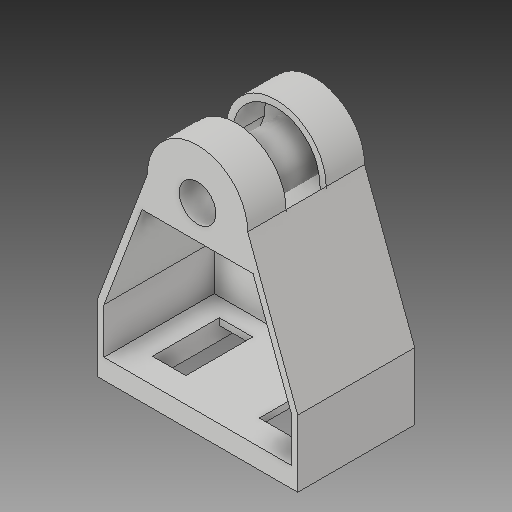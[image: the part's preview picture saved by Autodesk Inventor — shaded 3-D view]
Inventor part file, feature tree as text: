
AUTODESK INVENTOR PART (.ipt)
format: ipt  version: 2019 (Build 230136000, 136)  size: 250,368 bytes
history: native  units: mm
features: sketch x9, extrude x7, plane x2, shell x1, thicken_offset x1, hole x1, projected_geometry x1
ambient origin geometry x8: Origin, YZ Plane, XZ Plane, XY Plane, X Axis, Y Axis, Z Axis, Center Point
bodies: Solid1 (feature_tree)
feature tree (22):
  extrude  "Extrusion1"  Depth=5.5mm
  shell  "Shell2"  Thickness=17.5mm
  thicken_offset  "Thicken5"
  extrude  "Extrusion6"  Depth=30.0mm
  extrude  "Extrusion7"  Depth=2.0mm
  sketch  "Sketch14"  dims[d70=2.0mm d74=21.0mm]
  plane  "Work Plane2"
  hole  "Hole3"  [1 undecoded]
  extrude  "Extrusion9"  Depth=4.5mm
  extrude  "Extrusion10"  Depth=1.25mm
  plane  "Work Plane3"
  extrude  "Extrusion11"  Depth=5.0mm
  extrude  "Extrusion13"  Depth=2.5mm
  sketch  "Sketch1"  dims[d0=15.0mm d8=5.5mm d9=17.5mm d10=0.0mm]
  sketch  "Sketch12"  dims[d32=1.0mm d67=30.0mm]
  projected_geometry  "Projected Loop9"
  sketch  "Sketch13"  dims[d68=30.0mm d69=2.0mm]
  sketch  "Sketch16"  dims[d75=15.0mm d77=4.5mm]
  sketch  "Sketch17"  dims[d78=4.5mm d79=1.25mm]
  sketch  "Sketch18"  dims[d80=2.0mm d81=0.0mm d82=5.0mm]
  sketch  "Sketch19"  dims[d83=10.0mm d84=2.5mm]
  sketch  "Sketch22"  dims[d85=2.5mm d86=5.0mm d87=10.0mm d88=2.5mm d89=2.5mm d90=2.0mm d91=0.0mm d96=10.0mm d97=5.0mm d98=3.4mm d99=6.0mm d100=11.0mm d101=2.6mm d102=90.0deg d103=8.0mm d104=20.594885mm d105=9.5mm d106=2.0mm d107=0.0mm d108=5.5mm d109=2.0mm d110=0.0mm d111=15.0mm d112=6.0mm d113=4.0mm d114=0.0mm d117=5.0mm d118=2.0mm d119=0.0mm]
note: 1 required parameter value undecoded (feature->parameter linkage not recoverable at this tier; creation-order binding heuristic only, values carry confidence <= 0.55)
